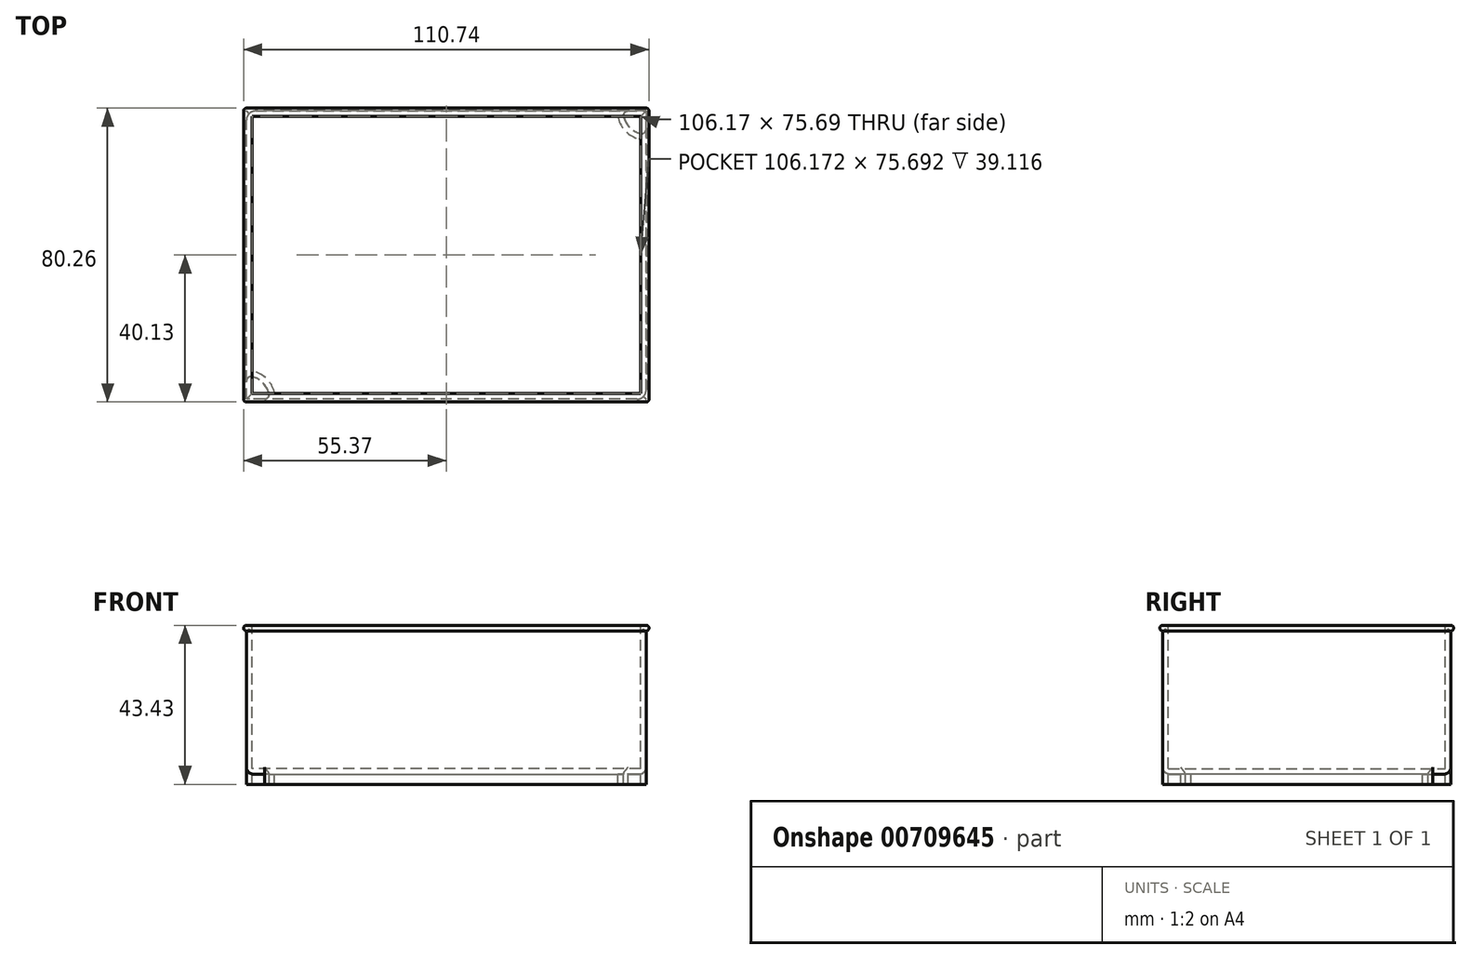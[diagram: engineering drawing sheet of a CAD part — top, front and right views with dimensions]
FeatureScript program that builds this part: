
annotation { "Feature Type Name" : "Feature", "Feature Type Description" : "" }
export const myFeature = defineFeature(function(context is Context, id is Id, definition is map)
    precondition{}
    {
        {
            var Q0;
            Q0=qCreatedBy(makeId("Front.planeOp"),FACE);
            var sketch = newSketch(context, id + "F0", { "sketchPlane" : qUnion([Q0])});
            skLineSegment(sketch, "E0.bottom", {"start": v(54.61, -20.32) * mm, "end": v(-54.61, -20.32) * mm});
            skLineSegment(sketch, "E0.top", {"start": v(54.61, 20.32) * mm, "end": v(-54.61, 20.32) * mm});
            skLineSegment(sketch, "E0.left", {"start": v(54.61, -20.32) * mm, "end": v(54.61, 20.32) * mm});
            skLineSegment(sketch, "E0.right", {"start": v(-54.61, -20.32) * mm, "end": v(-54.61, 20.32) * mm});
            skPoint(sketch, "E0.middle", {"position": v(0, 0) * mm});
            skSolve(sketch);
        }
        {
            var Q0;
            Q0=makeQuery(id+"F0.imprint","IMPRINT",FACE,{"disambiguationData":[TD([[makeQuery(id+"F0.imprint","IMPRINT",EDGE,{"derivedFrom":sQuery(id+"F0.wireOp",EDGE,"E0.bottom")}),-1.0]])]});
            extrude(context, id + "F1", {"entities" : qUnion([Q0]), "depth" : 78.74 * mm, "symmetric" : true});
        }
        {
            var Q0;
            Q0=makeQuery(id+"F1.opExtrude","SWEPT_FACE",FACE,{"disambiguationData":[OSD([sQuery(id+"F0.wireOp",EDGE,"E0.top")])]});
            shell(context, id + "F2", {"entities" : qUnion([Q0]), "thickness" : 1.52 * mm});
        }
        {
            var Q0;
            Q0=makeQuery(id+"F1.opExtrude","CAP_FACE",FACE,{"disambiguationData":[OSD([sQuery(id+"F0.wireOp",EDGE,"E0.bottom"),sQuery(id+"F0.wireOp",EDGE,"E0.top"),sQuery(id+"F0.wireOp",EDGE,"E0.left"),sQuery(id+"F0.wireOp",EDGE,"E0.right")])],"isStart":false});
            var sketch = newSketch(context, id + "F3", { "sketchPlane" : qUnion([Q0])});
            skArc(sketch, "E1", {"start": v(-54.61, 20.32) * mm, "mid": v(-55.37, 19.56) * mm, "end": v(-54.61, 18.8) * mm});
            skSolve(sketch);
        }
        {
            var Q0;
            {var subQ0=sQuery(id+"F3.wireOp",EDGE,"E1");Q0=makeQuery(id+"F3.imprint","IMPRINT",FACE,{"disambiguationData":[TD([[makeQuery(id+"F3.imprint","IMPRINT",EDGE,{"derivedFrom":subQ0}),1.0]])]});}
            var Q1;
            Q1=makeQuery(id+"F1.opExtrude","SWEPT_EDGE",EDGE,{"disambiguationData":[OSD([sQuery(id+"F0.wireOp",EDGE,"E0.top"),sQuery(id+"F0.wireOp",EDGE,"E0.right")])]});
            var Q2;
            Q2=makeQuery(id+"F1.opExtrude","CAP_EDGE",EDGE,{"disambiguationData":[OSD([sQuery(id+"F0.wireOp",EDGE,"E0.top")])],"isStart":true});
            var Q3;
            Q3=makeQuery(id+"F1.opExtrude","SWEPT_EDGE",EDGE,{"disambiguationData":[OSD([sQuery(id+"F0.wireOp",EDGE,"E0.top"),sQuery(id+"F0.wireOp",EDGE,"E0.left")])]});
            var Q4;
            Q4=makeQuery(id+"F1.opExtrude","CAP_EDGE",EDGE,{"disambiguationData":[OSD([sQuery(id+"F0.wireOp",EDGE,"E0.top")])],"isStart":false});
            sweep(context, id + "F4", {"operationType" : NewBodyOperationType.ADD, "profiles" : qUnion([Q0]), "path" : qUnion([Q1, Q2, Q3, Q4])});
        }
        {
            var Q0;
            Q0=makeQuery(id+"F1.opExtrude","SWEPT_FACE",FACE,{"disambiguationData":[OSD([sQuery(id+"F0.wireOp",EDGE,"E0.bottom")])]});
            var sketch = newSketch(context, id + "F5", { "sketchPlane" : qUnion([Q0])});
            skLineSegment(sketch, "E2.bottom", {"start": v(54.61, 39.37) * mm, "end": v(49.7, 39.37) * mm});
            skLineSegment(sketch, "E2.left", {"start": v(54.61, 39.37) * mm, "end": v(54.61, 34.45) * mm});
            skPoint(sketch, "E3.newPointA", {"position": v(48.26, 19.05) * mm});
            skArc(sketch, "E4", {"start": v(48.46, 37.78) * mm, "mid": v(50.12, 34.88) * mm, "end": v(53.02, 33.22) * mm});
            skPoint(sketch, "E5.visualSharp", {"position": v(48.26, 39.37) * mm});
            skArc(sketch, "E5.filletArc", {"start": v(49.7, 39.37) * mm, "mid": v(48.69, 38.88) * mm, "end": v(48.46, 37.78) * mm});
            skPoint(sketch, "E6.visualSharp", {"position": v(54.61, 33.02) * mm});
            skArc(sketch, "E6.filletArc", {"start": v(53.02, 33.22) * mm, "mid": v(54.12, 33.45) * mm, "end": v(54.6, 34.45) * mm});
            skArc(sketch, "E7.MirrorCS", {"start": v(-49.7, 39.37) * mm, "mid": v(-48.69, 38.88) * mm, "end": v(-48.46, 37.78) * mm});
            skArc(sketch, "E8.MirrorCS", {"start": v(-48.46, 37.78) * mm, "mid": v(-50.12, 34.88) * mm, "end": v(-53.02, 33.22) * mm});
            skArc(sketch, "E9.MirrorCS", {"start": v(-53.02, 33.22) * mm, "mid": v(-54.12, 33.45) * mm, "end": v(-54.6, 34.45) * mm});
            skLineSegment(sketch, "E10.MirrorCS", {"start": v(-54.61, 39.37) * mm, "end": v(-54.61, 34.45) * mm});
            skLineSegment(sketch, "E11.MirrorCS", {"start": v(-54.61, 39.37) * mm, "end": v(-49.7, 39.37) * mm});
            skArc(sketch, "E12.MirrorCS", {"start": v(-48.46, -37.78) * mm, "mid": v(-50.12, -34.88) * mm, "end": v(-53.02, -33.22) * mm});
            skArc(sketch, "E13.MirrorCS", {"start": v(-49.7, -39.37) * mm, "mid": v(-48.69, -38.88) * mm, "end": v(-48.46, -37.78) * mm});
            skLineSegment(sketch, "E14.MirrorCS", {"start": v(-54.6, -39.37) * mm, "end": v(-49.7, -39.37) * mm});
            skLineSegment(sketch, "E15.MirrorCS", {"start": v(-54.6, -39.37) * mm, "end": v(-54.6, -34.45) * mm});
            skArc(sketch, "E16.MirrorCS", {"start": v(-53.02, -33.22) * mm, "mid": v(-54.12, -33.45) * mm, "end": v(-54.6, -34.45) * mm});
            skArc(sketch, "E17.MirrorCS", {"start": v(49.7, -39.37) * mm, "mid": v(48.69, -38.88) * mm, "end": v(48.46, -37.78) * mm});
            skArc(sketch, "E18.MirrorCS", {"start": v(48.46, -37.78) * mm, "mid": v(50.12, -34.88) * mm, "end": v(53.02, -33.22) * mm});
            skArc(sketch, "E19.MirrorCS", {"start": v(53.02, -33.22) * mm, "mid": v(54.12, -33.45) * mm, "end": v(54.6, -34.45) * mm});
            skLineSegment(sketch, "E20.MirrorCS", {"start": v(54.6, -39.37) * mm, "end": v(54.6, -34.45) * mm});
            skLineSegment(sketch, "E21.MirrorCS", {"start": v(54.6, -39.37) * mm, "end": v(49.7, -39.37) * mm});
            skSolve(sketch);
        }
        {
            var Q0;
            Q0=makeQuery(id+"F5.imprint","IMPRINT",FACE,{"disambiguationData":[TD([[makeQuery(id+"F5.imprint","IMPRINT",EDGE,{"derivedFrom":sQuery(id+"F5.wireOp",EDGE,"E2.bottom")}),1.0]])]});
            var Q1;
            Q1=makeQuery(id+"F5.imprint","IMPRINT",FACE,{"disambiguationData":[TD([[makeQuery(id+"F5.imprint","IMPRINT",EDGE,{"derivedFrom":sQuery(id+"F5.wireOp",EDGE,"E8.MirrorCS")}),-1.0]])]});
            var Q2;
            Q2=makeQuery(id+"F5.imprint","IMPRINT",FACE,{"disambiguationData":[TD([[makeQuery(id+"F5.imprint","IMPRINT",EDGE,{"derivedFrom":sQuery(id+"F5.wireOp",EDGE,"E12.MirrorCS")}),1.0]])]});
            var Q3;
            Q3=makeQuery(id+"F5.imprint","IMPRINT",FACE,{"disambiguationData":[TD([[makeQuery(id+"F5.imprint","IMPRINT",EDGE,{"derivedFrom":sQuery(id+"F5.wireOp",EDGE,"E17.MirrorCS")}),-1.0]])]});
            extrude(context, id + "F6", {"entities" : qUnion([Q0, Q1, Q2, Q3]), "operationType" : NewBodyOperationType.ADD, "depth" : 2.8 * mm});
        }
        {
            var Q0;
            Q0=makeQuery(id+"F6.opExtrude","CAP_FACE",FACE,{"disambiguationData":[OSD([sQuery(id+"F5.wireOp",EDGE,"E2.bottom"),sQuery(id+"F5.wireOp",EDGE,"E2.left"),sQuery(id+"F5.wireOp",EDGE,"E4"),sQuery(id+"F5.wireOp",EDGE,"E5.filletArc"),sQuery(id+"F5.wireOp",EDGE,"E6.filletArc")])],"isStart":false});
            var Q1;
            Q1=makeQuery(id+"F6.opExtrude","CAP_FACE",FACE,{"disambiguationData":[OSD([sQuery(id+"F5.wireOp",EDGE,"E8.MirrorCS"),sQuery(id+"F5.wireOp",EDGE,"E9.MirrorCS"),sQuery(id+"F5.wireOp",EDGE,"E10.MirrorCS"),sQuery(id+"F5.wireOp",EDGE,"E7.MirrorCS"),sQuery(id+"F5.wireOp",EDGE,"E11.MirrorCS")])],"isStart":false});
            var Q2;
            Q2=makeQuery(id+"F6.opExtrude","CAP_FACE",FACE,{"disambiguationData":[OSD([sQuery(id+"F5.wireOp",EDGE,"E12.MirrorCS"),sQuery(id+"F5.wireOp",EDGE,"E13.MirrorCS"),sQuery(id+"F5.wireOp",EDGE,"E14.MirrorCS"),sQuery(id+"F5.wireOp",EDGE,"E15.MirrorCS"),sQuery(id+"F5.wireOp",EDGE,"E16.MirrorCS")])],"isStart":false});
            var Q3;
            Q3=makeQuery(id+"F6.opExtrude","CAP_FACE",FACE,{"disambiguationData":[OSD([sQuery(id+"F5.wireOp",EDGE,"E17.MirrorCS"),sQuery(id+"F5.wireOp",EDGE,"E18.MirrorCS"),sQuery(id+"F5.wireOp",EDGE,"E19.MirrorCS"),sQuery(id+"F5.wireOp",EDGE,"E20.MirrorCS"),sQuery(id+"F5.wireOp",EDGE,"E21.MirrorCS")])],"isStart":false});
            shell(context, id + "F7", {"entities" : qUnion([Q0, Q1, Q2, Q3]), "thickness" : 1.52 * mm});
        }
        {
            var Q0;
            Q0=makeQuery(id+"F1.opExtrude","SWEPT_EDGE",EDGE,{"disambiguationData":[OSD([sQuery(id+"F0.wireOp",EDGE,"E0.bottom"),sQuery(id+"F0.wireOp",EDGE,"E0.right")])]});
            var Q1;
            Q1=makeQuery(id+"F1.opExtrude","CAP_EDGE",EDGE,{"disambiguationData":[OSD([sQuery(id+"F0.wireOp",EDGE,"E0.bottom")])],"isStart":false});
            var Q2;
            Q2=makeQuery(id+"F1.opExtrude","SWEPT_EDGE",EDGE,{"disambiguationData":[OSD([sQuery(id+"F0.wireOp",EDGE,"E0.bottom"),sQuery(id+"F0.wireOp",EDGE,"E0.left")])]});
            var Q3;
            Q3=makeQuery(id+"F1.opExtrude","CAP_EDGE",EDGE,{"disambiguationData":[OSD([sQuery(id+"F0.wireOp",EDGE,"E0.bottom")])],"isStart":true});
            fillet(context, id + "F8", {"entities" : qUnion([Q0, Q1, Q2, Q3]), "radius" : 1.9 * mm, "tangentPropagation" : true, "allowEdgeOverflow" : false});
        }
        {
            var Q0;
            Q0=makeQuery(id+"F4.opSweep","MID_CAP_EDGE",EDGE,{"disambiguationData":[OSD([sQuery(id+"F0.wireOp",EDGE,"E0.top"),sQuery(id+"F0.wireOp",EDGE,"E0.left"),sQuery(id+"F3.wireOp",EDGE,"E1")])],"capPos":3.0});
            var Q1;
            Q1=makeQuery(id+"F4.opSweep","MID_CAP_EDGE",EDGE,{"disambiguationData":[OSD([sQuery(id+"F0.wireOp",EDGE,"E0.top"),sQuery(id+"F0.wireOp",EDGE,"E0.left"),sQuery(id+"F3.wireOp",EDGE,"E1")])],"capPos":2.0});
            var Q2;
            Q2=makeQuery(id+"F4.opSweep","MID_CAP_EDGE",EDGE,{"disambiguationData":[OSD([sQuery(id+"F0.wireOp",EDGE,"E0.top"),sQuery(id+"F0.wireOp",EDGE,"E0.right"),sQuery(id+"F3.wireOp",EDGE,"E1")])],"capPos":1.0});
            var Q3;
            Q3=makeQuery(id+"F4.opSweep","CAP_EDGE",EDGE,{"disambiguationData":[OSD([sQuery(id+"F0.wireOp",EDGE,"E0.top"),sQuery(id+"F0.wireOp",EDGE,"E0.right"),sQuery(id+"F3.wireOp",EDGE,"E1")])],"isStart":true});
            fillet(context, id + "F9", {"entities" : qUnion([Q0, Q1, Q2, Q3]), "radius" : 0.76 * mm, "tangentPropagation" : true, "allowEdgeOverflow" : false});
        }
        {
            var Q0;
            Q0=makeQuery(id+"F6.boolean.opBoolean","MERGE",EDGE,{"derivedFrom":[makeQuery(id+"F1.opExtrude","CAP_EDGE",EDGE,{"disambiguationData":[OSD([sQuery(id+"F0.wireOp",EDGE,"E0.left")])],"isStart":false}),makeQuery(id+"F6.opExtrude","SWEPT_EDGE",EDGE,{"disambiguationData":[OSD([sQuery(id+"F5.wireOp",EDGE,"E2.bottom"),sQuery(id+"F5.wireOp",EDGE,"E2.left")])]})]});
            var Q1;
            Q1=makeQuery(id+"F6.boolean.opBoolean","MERGE",EDGE,{"derivedFrom":[makeQuery(id+"F1.opExtrude","CAP_EDGE",EDGE,{"disambiguationData":[OSD([sQuery(id+"F0.wireOp",EDGE,"E0.left")])],"isStart":true}),makeQuery(id+"F6.opExtrude","SWEPT_EDGE",EDGE,{"disambiguationData":[OSD([sQuery(id+"F5.wireOp",EDGE,"E20.MirrorCS"),sQuery(id+"F5.wireOp",EDGE,"E21.MirrorCS")])]})]});
            var Q2;
            Q2=makeQuery(id+"F6.boolean.opBoolean","MERGE",EDGE,{"derivedFrom":[makeQuery(id+"F1.opExtrude","CAP_EDGE",EDGE,{"disambiguationData":[OSD([sQuery(id+"F0.wireOp",EDGE,"E0.right")])],"isStart":false}),makeQuery(id+"F6.opExtrude","SWEPT_EDGE",EDGE,{"disambiguationData":[OSD([sQuery(id+"F5.wireOp",EDGE,"E10.MirrorCS"),sQuery(id+"F5.wireOp",EDGE,"E11.MirrorCS")])]})]});
            var Q3;
            Q3=makeQuery(id+"F6.boolean.opBoolean","MERGE",EDGE,{"derivedFrom":[makeQuery(id+"F1.opExtrude","CAP_EDGE",EDGE,{"disambiguationData":[OSD([sQuery(id+"F0.wireOp",EDGE,"E0.right")])],"isStart":true}),makeQuery(id+"F6.opExtrude","SWEPT_EDGE",EDGE,{"disambiguationData":[OSD([sQuery(id+"F5.wireOp",EDGE,"E14.MirrorCS"),sQuery(id+"F5.wireOp",EDGE,"E15.MirrorCS")])]})]});
            fillet(context, id + "F10", {"entities" : qUnion([Q0, Q1, Q2, Q3]), "radius" : 2.54 * mm, "tangentPropagation" : true, "allowEdgeOverflow" : false});
        }
    });
